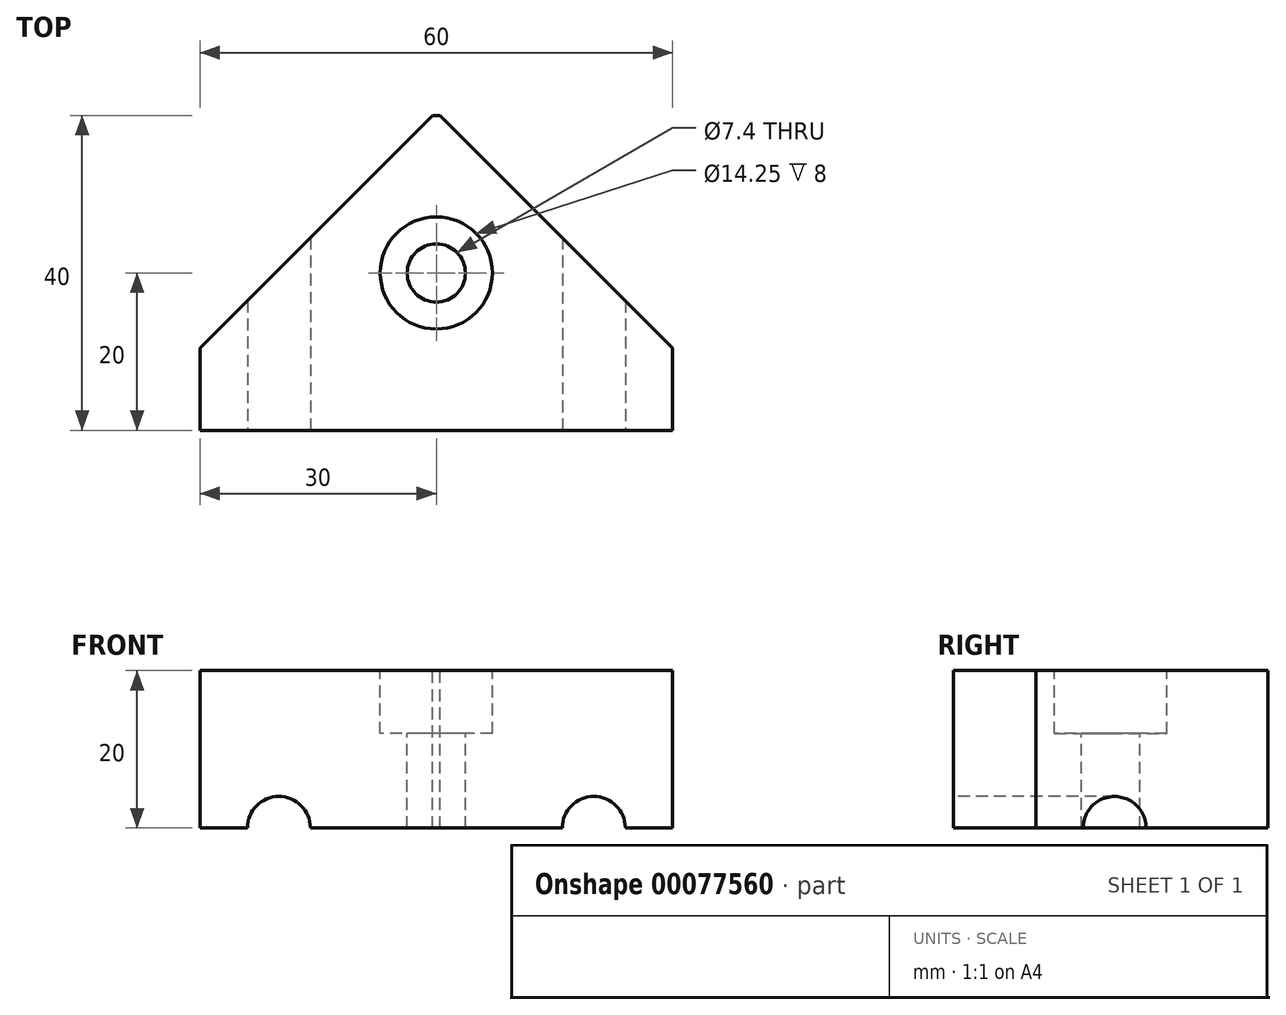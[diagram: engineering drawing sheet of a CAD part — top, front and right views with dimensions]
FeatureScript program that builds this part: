
annotation { "Feature Type Name" : "Feature", "Feature Type Description" : "" }
export const myFeature = defineFeature(function(context is Context, id is Id, definition is map)
    precondition{}
    {
        {
            var Q0;
            Q0=qCreatedBy(makeId("Front.planeOp"),FACE);
            var sketch = newSketch(context, id + "F0", { "sketchPlane" : qUnion([Q0])});
            skLineSegment(sketch, "E0.bottom", {"start": v(30, 10) * mm, "end": v(-30, 10) * mm});
            skLineSegment(sketch, "E0.top", {"start": v(30, -10) * mm, "end": v(-30, -10) * mm});
            skLineSegment(sketch, "E0.left", {"start": v(30, 10) * mm, "end": v(30, -10) * mm});
            skLineSegment(sketch, "E0.right", {"start": v(-30, 10) * mm, "end": v(-30, -10) * mm});
            skPoint(sketch, "E0.middle", {"position": v(0, 0) * mm});
            skSolve(sketch);
        }
        {
            var Q0;
            Q0 = qSketchRegion(id + "F0", true);
            extrude(context, id + "F1", {"entities" : qUnion([Q0]), "oppositeDirection" : true, "depth" : 40 * mm});
        }
        {
            var Q0;
            Q0=makeQuery(id+"F1.opExtrude","SWEPT_FACE",FACE,{"disambiguationData":[OSD([sQuery(id+"F0.wireOp",EDGE,"E0.bottom")])]});
            var sketch = newSketch(context, id + "F2", { "sketchPlane" : qUnion([Q0])});
            skLineSegment(sketch, "E1", {"start": v(-0.5, 40) * mm, "end": v(0.5, 40) * mm});
            skLineSegment(sketch, "E2", {"start": v(0.5, 40) * mm, "end": v(30, 10.5) * mm});
            skLineSegment(sketch, "E3", {"start": v(30, 10.5) * mm, "end": v(30, 70.5) * mm});
            skLineSegment(sketch, "E4", {"start": v(30, 70.5) * mm, "end": v(-30, 70.5) * mm});
            skLineSegment(sketch, "E5", {"start": v(-30, 70.5) * mm, "end": v(-30, 10.5) * mm});
            skLineSegment(sketch, "E6", {"start": v(-30, 10.5) * mm, "end": v(-0.5, 40) * mm});
            skSolve(sketch);
        }
        {
            var Q0;
            {var subQ4=sQuery(id+"F2.wireOp",EDGE,"E6");Q0=makeQuery(id+"F2.imprint","IMPRINT",FACE,{"disambiguationData":[TD([[makeQuery(id+"F2.imprint","IMPRINT",EDGE,{"derivedFrom":subQ4}),1.0]])]});}
            var Q1;
            {var subQ0=sQuery(id+"F2.wireOp",EDGE,"E2");Q1=makeQuery(id+"F2.imprint","IMPRINT",FACE,{"disambiguationData":[TD([[makeQuery(id+"F2.imprint","IMPRINT",EDGE,{"derivedFrom":subQ0}),1.0]])]});}
            extrude(context, id + "F3", {"entities" : qUnion([Q0, Q1]), "operationType" : NewBodyOperationType.REMOVE, "endBound" : BoundingType.THROUGH_ALL, "oppositeDirection" : true, "depth" : 25 * mm});
        }
        {
            var Q0;
            Q0=makeQuery(id+"F1.opExtrude","CAP_FACE",FACE,{"disambiguationData":[OSD([sQuery(id+"F0.wireOp",EDGE,"E0.bottom"),sQuery(id+"F0.wireOp",EDGE,"E0.top"),sQuery(id+"F0.wireOp",EDGE,"E0.left"),sQuery(id+"F0.wireOp",EDGE,"E0.right")])],"isStart":true});
            var sketch = newSketch(context, id + "F4", { "sketchPlane" : qUnion([Q0])});
            skCircle(sketch, "E7", {"center": v(-20, -10) * mm, "radius": 4 * mm});
            skCircle(sketch, "E8.MirrorC", {"center": v(20, -10) * mm, "radius": 4 * mm});
            skSolve(sketch);
        }
        {
            var Q0;
            Q0 = qSketchRegion(id + "F4", true);
            extrude(context, id + "F5", {"entities" : qUnion([Q0]), "operationType" : NewBodyOperationType.REMOVE, "endBound" : BoundingType.THROUGH_ALL, "oppositeDirection" : true, "depth" : 25 * mm});
        }
        {
            var Q0;
            Q0=makeQuery(id+"F1.opExtrude","SWEPT_FACE",FACE,{"disambiguationData":[OSD([sQuery(id+"F0.wireOp",EDGE,"E0.bottom")])]});
            var sketch = newSketch(context, id + "F6", { "sketchPlane" : qUnion([Q0])});
            skPoint(sketch, "E9", {"position": v(0, 20) * mm});
            skSolve(sketch);
        }
        {
            var Q0;
            Q0=sQuery(id+"F6.wireOp",VERTEX,"E9");
            var Q1;
            Q1=makeQuery(id+"F1.opExtrude","SWEPT_BODY",BODY,{"disambiguationData":[OSD([sQuery(id+"F0.wireOp",EDGE,"E0.bottom"),sQuery(id+"F0.wireOp",EDGE,"E0.top"),sQuery(id+"F0.wireOp",EDGE,"E0.left"),sQuery(id+"F0.wireOp",EDGE,"E0.right")])]});
            hole(context, id + "F7", {"style" : HoleStyle.C_BORE, "endStyle" : HoleEndStyle.BLIND, "standardTappedOrClearance" : lookupTablePath({ "standard" : "ISO", "engagement" : "25%", "pitch" : "1 mm", "size" : "M8", "type" : "Tapped" }), "standardBlindInLast" : lookupTablePath({ "standard" : "ISO", "engagement" : "25%", "pitch" : "1 mm", "size" : "M8", "type" : "Tapped" }), "holeDiameter" : 7.4 * mm, "cBoreDiameter" : 14.25 * mm, "cBoreDepth" : 8 * mm, "holeDepth" : 30 * mm, "startFromSketch" : true, "locations" : qUnion([Q0]), "scope" : qUnion([Q1])});
        }
    });
